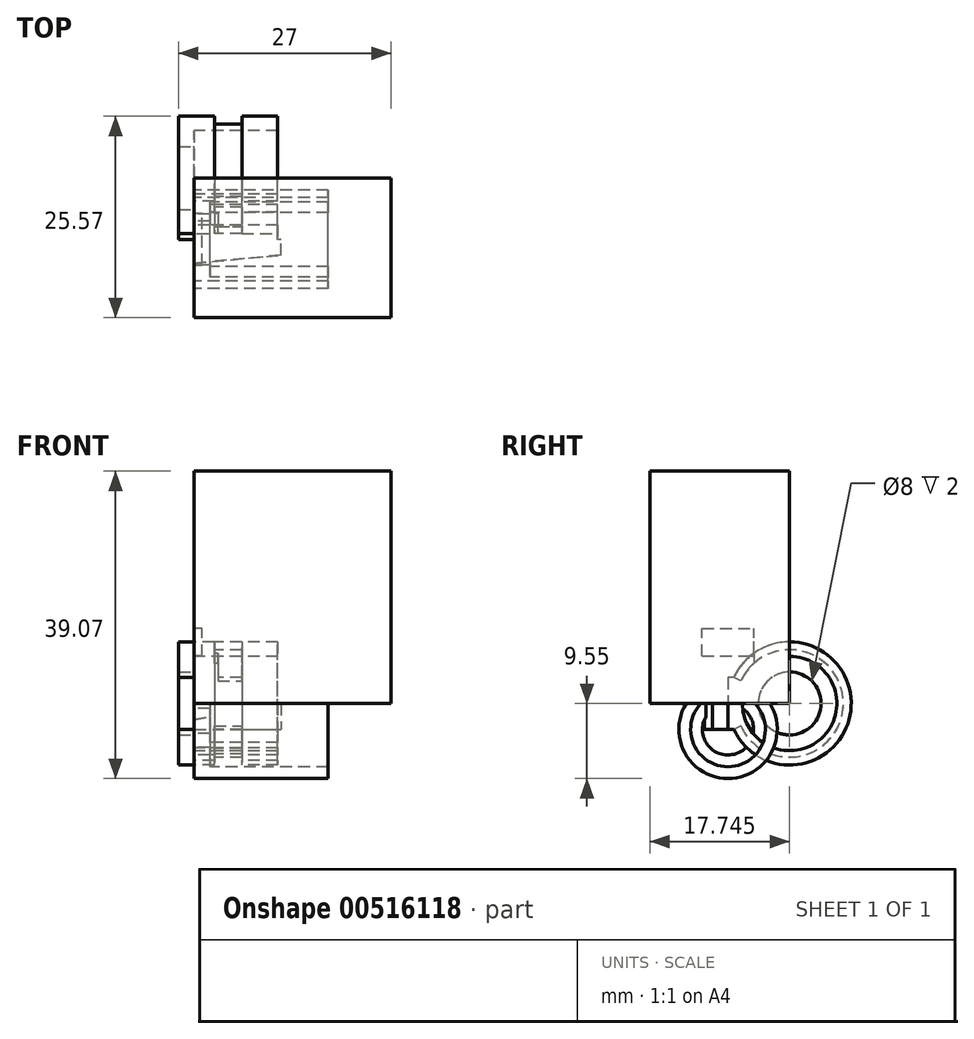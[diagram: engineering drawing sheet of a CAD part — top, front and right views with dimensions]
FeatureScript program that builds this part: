
annotation { "Feature Type Name" : "Feature", "Feature Type Description" : "" }
export const myFeature = defineFeature(function(context is Context, id is Id, definition is map)
    precondition{}
    {
        {
            var Q0;
            Q0=qCreatedBy(makeId("Top.planeOp"),FACE);
            var sketch = newSketch(context, id + "F0", { "sketchPlane" : qUnion([Q0])});
            skLineSegment(sketch, "E0", {"start": v(0, 0) * mm, "end": v(11, 0) * mm});
            skLineSegment(sketch, "E1", {"start": v(11, 0) * mm, "end": v(11, -2) * mm});
            skLineSegment(sketch, "E2", {"start": v(0, 0) * mm, "end": v(0, -3) * mm});
            skLineSegment(sketch, "E3", {"start": v(0, -3) * mm, "end": v(11, -2) * mm});
            skSolve(sketch);
        }
        {
            var Q0;
            Q0=makeQuery(id+"F0.imprint","IMPRINT",FACE,{"disambiguationData":[TD([[makeQuery(id+"F0.imprint","IMPRINT",EDGE,{"derivedFrom":sQuery(id+"F0.wireOp",EDGE,"E0")}),-1.0]])]});
            extrude(context, id + "F1", {"entities" : qUnion([Q0]), "depth" : 6.6 * mm, "offsetDistance" : 25 * mm});
        }
        {
            var Q0;
            Q0=qCreatedBy(makeId("Right.planeOp"),FACE);
            var sketch = newSketch(context, id + "F2", { "sketchPlane" : qUnion([Q0])});
            skLineSegment(sketch, "E4.0", {"start": v(0, 6.6) * mm, "end": v(0, 0) * mm});
            skLineSegment(sketch, "E5", {"start": v(0, 3.3) * mm, "end": v(7.83, 3.3) * mm, "construction": true});
            skCircle(sketch, "E6", {"center": v(7.83, 3.3) * mm, "radius": 7.83 * mm});
            skCircle(sketch, "E7", {"center": v(7.83, 3.3) * mm, "radius": 6 * mm});
            skCircle(sketch, "E8", {"center": v(7.83, 3.3) * mm, "radius": 4 * mm});
            skSolve(sketch);
        }
        {
            var Q0;
            Q0=makeQuery(id+"F2.imprint","IMPRINT",FACE,{"disambiguationData":[TD([[makeQuery(id+"F2.imprint","IMPRINT",EDGE,{"derivedFrom":sQuery(id+"F2.wireOp",EDGE,"E6")}),1.0]])]});
            extrude(context, id + "F3", {"entities" : qUnion([Q0]), "depth" : 10.6 * mm, "offsetDistance" : 25 * mm});
        }
        {
            var Q0;
            Q0=makeQuery(id+"F2.imprint","IMPRINT",FACE,{"disambiguationData":[TD([[makeQuery(id+"F2.imprint","IMPRINT",EDGE,{"derivedFrom":sQuery(id+"F2.wireOp",EDGE,"E7")}),1.0]])]});
            var Q1;
            Q1=makeQuery(id+"F2.imprint","IMPRINT",FACE,{"disambiguationData":[TD([[makeQuery(id+"F2.imprint","IMPRINT",EDGE,{"derivedFrom":sQuery(id+"F2.wireOp",EDGE,"E6")}),1.0]])]});
            extrude(context, id + "F4", {"entities" : qUnion([Q0, Q1]), "operationType" : NewBodyOperationType.ADD, "oppositeDirection" : true, "depth" : 2 * mm, "offsetDistance" : 25 * mm});
        }
        {
            var Q0;
            Q0=qCreatedBy(makeId("Top.planeOp"),FACE);
            var sketch = newSketch(context, id + "F5", { "sketchPlane" : qUnion([Q0])});
            skLineSegment(sketch, "E9.0", {"start": v(-2, 15.65) * mm, "end": v(-2, 0) * mm});
            skLineSegment(sketch, "E9.1", {"start": v(10.6, 15.65) * mm, "end": v(10.6, 0) * mm});
            skLineSegment(sketch, "E10", {"start": v(-2, 15.65) * mm, "end": v(10.6, 15.65) * mm});
            skLineSegment(sketch, "E11.bottom", {"start": v(6.05, 14.65) * mm, "end": v(2.55, 14.65) * mm});
            skLineSegment(sketch, "E11.top", {"start": v(6.05, 16.65) * mm, "end": v(2.55, 16.65) * mm});
            skLineSegment(sketch, "E11.left", {"start": v(6.05, 14.65) * mm, "end": v(6.05, 16.65) * mm});
            skLineSegment(sketch, "E11.right", {"start": v(2.55, 14.65) * mm, "end": v(2.55, 16.65) * mm});
            skPoint(sketch, "E11.middle", {"position": v(4.3, 15.65) * mm});
            skSolve(sketch);
        }
        {
            var Q0;
            Q0=qCreatedBy(makeId("Right.planeOp"),FACE);
            var sketch = newSketch(context, id + "F6", { "sketchPlane" : qUnion([Q0])});
            skPoint(sketch, "E12.0", {"position": v(7.83, 3.3) * mm});
            skLineSegment(sketch, "E13.bottom", {"start": v(7.82, 3.3) * mm, "end": v(-9.92, 3.3) * mm});
            skLineSegment(sketch, "E13.top", {"start": v(7.82, 32.82) * mm, "end": v(-9.92, 32.82) * mm});
            skLineSegment(sketch, "E13.left", {"start": v(7.83, 3.3) * mm, "end": v(7.83, 32.82) * mm});
            skLineSegment(sketch, "E13.right", {"start": v(-9.92, 3.3) * mm, "end": v(-9.92, 32.82) * mm});
            skSolve(sketch);
        }
        {
            var Q0;
            Q0=makeQuery(id+"F6.imprint","IMPRINT",FACE,{"disambiguationData":[TD([[makeQuery(id+"F6.imprint","IMPRINT",EDGE,{"derivedFrom":sQuery(id+"F6.wireOp",EDGE,"E13.bottom")}),-1.0]])]});
            extrude(context, id + "F7", {"entities" : qUnion([Q0]), "depth" : 25 * mm, "offsetDistance" : 25 * mm});
        }
        {
            var Q0;
            Q0=makeQuery(id+"F7.opExtrude","SWEPT_FACE",FACE,{"disambiguationData":[OSD([sQuery(id+"F6.wireOp",EDGE,"E13.bottom")])]});
            var sketch = newSketch(context, id + "F8", { "sketchPlane" : qUnion([Q0])});
            skLineSegment(sketch, "E14.0.0", {"start": v(6.05, -15.65) * mm, "end": v(2.55, -15.65) * mm});
            skLineSegment(sketch, "E14.0.1", {"start": v(2.55, -15.65) * mm, "end": v(2.55, -14.65) * mm});
            skLineSegment(sketch, "E14.0.2", {"start": v(2.55, -14.65) * mm, "end": v(6.05, -14.65) * mm});
            skLineSegment(sketch, "E14.0.3", {"start": v(6.05, -14.65) * mm, "end": v(6.05, -15.65) * mm});
            skSolve(sketch);
        }
        {
            var Q0;
            Q0=makeQuery(id+"F8.imprint","IMPRINT",FACE,{"disambiguationData":[TD([[makeQuery(id+"F8.imprint","IMPRINT",EDGE,{"derivedFrom":sQuery(id+"F8.wireOp",EDGE,"E14.0.0")}),-1.0]])]});
            var Q1;
            Q1=makeQuery(id+"F7.opExtrude","SWEPT_EDGE",EDGE,{"disambiguationData":[OSD([sQuery(id+"F6.wireOp",EDGE,"E13.bottom"),sQuery(id+"F6.wireOp",EDGE,"E13.left")])]});
            revolve(context, id + "F9", {"operationType" : NewBodyOperationType.REMOVE, "entities" : qUnion([Q0]), "axis" : qUnion([Q1]), "revolveType" : RevolveType.TWO_DIRECTIONS, "oppositeDirection" : true, "angle" : 155 * degree, "angleBack" : 205 * degree});
        }
        {
            var Q0;
            Q0=makeQuery(id+"F3.opExtrude","CAP_FACE",FACE,{"disambiguationData":[OSD([sQuery(id+"F2.wireOp",EDGE,"E6"),sQuery(id+"F2.wireOp",EDGE,"E7")])],"isStart":false});
            var sketch = newSketch(context, id + "F10", { "sketchPlane" : qUnion([Q0])});
            skPoint(sketch, "E15.0", {"position": v(0.73, 6.6) * mm});
            skPoint(sketch, "E15.1", {"position": v(0.73, 0) * mm});
            skLineSegment(sketch, "E16", {"start": v(0.73, 6.6) * mm, "end": v(0, 6.6) * mm});
            skLineSegment(sketch, "E17", {"start": v(0, 6.6) * mm, "end": v(0, 0) * mm});
            skLineSegment(sketch, "E18", {"start": v(0, 0) * mm, "end": v(0.73, 0) * mm});
            skLineSegment(sketch, "E19", {"start": v(0.73, 0) * mm, "end": v(0.73, 6.6) * mm});
            skSolve(sketch);
        }
        {
            var Q0;
            {var subQ0=sQuery(id+"F10.wireOp",EDGE,"E19");Q0=makeQuery(id+"F10.imprint","IMPRINT",FACE,{"disambiguationData":[TD([[makeQuery(id+"F10.imprint","IMPRINT",EDGE,{"derivedFrom":subQ0}),1.0]])]});}
            var Q1;
            {var subQ0=sQuery(id+"F10.wireOp",EDGE,"E16");Q1=makeQuery(id+"F10.imprint","IMPRINT",FACE,{"disambiguationData":[TD([[makeQuery(id+"F10.imprint","IMPRINT",EDGE,{"derivedFrom":subQ0}),1.0]])]});}
            var Q2;
            {var subQ0=sQuery(id+"F10.wireOp",EDGE,"E18");Q2=makeQuery(id+"F10.imprint","IMPRINT",FACE,{"disambiguationData":[TD([[makeQuery(id+"F10.imprint","IMPRINT",EDGE,{"derivedFrom":subQ0}),1.0]])]});}
            var Q3;
            Q3=makeQuery(id+"F4.opExtrude","CAP_FACE",FACE,{"disambiguationData":[OSD([sQuery(id+"F2.wireOp",EDGE,"E6"),sQuery(id+"F2.wireOp",EDGE,"E8")])],"isStart":false});
            extrude(context, id + "F11", {"entities" : qUnion([Q0, Q1, Q2]), "operationType" : NewBodyOperationType.ADD, "endBound" : BoundingType.UP_TO_SURFACE, "oppositeDirection" : true, "depth" : 25 * mm, "endBoundEntityFace" : qUnion([Q3]), "offsetDistance" : 25 * mm});
        }
        {
            var Q0;
            Q0=qCreatedBy(makeId("Right.planeOp"),FACE);
            var sketch = newSketch(context, id + "F12", { "sketchPlane" : qUnion([Q0])});
            skCircle(sketch, "E20", {"center": v(0, 0) * mm, "radius": 4.75 * mm});
            skCircle(sketch, "E21", {"center": v(0, 0) * mm, "radius": 6.25 * mm});
            skCircle(sketch, "E22", {"center": v(0, 0) * mm, "radius": 3.25 * mm});
            skSolve(sketch);
        }
        {
            var Q0;
            Q0=makeQuery(id+"F12.imprint","IMPRINT",FACE,{"disambiguationData":[TD([[makeQuery(id+"F12.imprint","IMPRINT",EDGE,{"derivedFrom":sQuery(id+"F12.wireOp",EDGE,"E20")}),-1.0]])]});
            extrude(context, id + "F13", {"entities" : qUnion([Q0]), "depth" : 17 * mm, "offsetDistance" : 25 * mm});
        }
        {
            var Q0;
            Q0=makeQuery(id+"F12.imprint","IMPRINT",FACE,{"disambiguationData":[TD([[makeQuery(id+"F12.imprint","IMPRINT",EDGE,{"derivedFrom":sQuery(id+"F12.wireOp",EDGE,"E20")}),1.0]])]});
            extrude(context, id + "F14", {"entities" : qUnion([Q0]), "operationType" : NewBodyOperationType.ADD, "depth" : 2 * mm, "offsetDistance" : 25 * mm});
        }
        {
            var Q0;
            Q0=makeQuery(id+"F13.opExtrude","CAP_FACE",FACE,{"disambiguationData":[OSD([sQuery(id+"F12.wireOp",EDGE,"E20"),sQuery(id+"F12.wireOp",EDGE,"E21")])],"isStart":false});
            var sketch = newSketch(context, id + "F15", { "sketchPlane" : qUnion([Q0])});
            skPoint(sketch, "E23", {"position": v(-6.25, 0) * mm});
            skPoint(sketch, "E24", {"position": v(6.25, 0) * mm});
            skLineSegment(sketch, "E25.bottom", {"start": v(-6.25, 0) * mm, "end": v(6.25, 0) * mm});
            skLineSegment(sketch, "E25.top", {"start": v(-6.25, 16.25) * mm, "end": v(6.25, 16.25) * mm});
            skLineSegment(sketch, "E25.left", {"start": v(-6.25, 0) * mm, "end": v(-6.25, 16.25) * mm});
            skLineSegment(sketch, "E25.right", {"start": v(6.25, 0) * mm, "end": v(6.25, 16.25) * mm});
            skSolve(sketch);
        }
        {
            var Q0;
            Q0=makeQuery(id+"F12.imprint","IMPRINT",FACE,{"disambiguationData":[TD([[makeQuery(id+"F12.imprint","IMPRINT",EDGE,{"derivedFrom":sQuery(id+"F12.wireOp",EDGE,"E20")}),-1.0]])]});
            var sketch = newSketch(context, id + "F16", { "sketchPlane" : qUnion([Q0])});
            skArc(sketch, "E26.0.0", {"start": v(-6.25, 0) * mm, "mid": v(0, 6.25) * mm, "end": v(6.25, 0) * mm});
            skLineSegment(sketch, "E26.0.1", {"start": v(6.25, 0) * mm, "end": v(6.25, 16.25) * mm});
            skLineSegment(sketch, "E26.0.2", {"start": v(6.25, 16.25) * mm, "end": v(-6.25, 16.25) * mm});
            skLineSegment(sketch, "E26.0.3", {"start": v(-6.25, 16.25) * mm, "end": v(-6.25, 0) * mm});
            skSolve(sketch);
        }
        {
            var Q0;
            Q0=makeQuery(id+"F16.imprint","IMPRINT",FACE,{"disambiguationData":[TD([[makeQuery(id+"F16.imprint","IMPRINT",EDGE,{"derivedFrom":sQuery(id+"F16.wireOp",EDGE,"E26.0.0")}),-1.0]])]});
            var sketch = newSketch(context, id + "F17", { "sketchPlane" : qUnion([Q0])});
            skLineSegment(sketch, "E27.bottom", {"start": v(-6.33, 12.82) * mm, "end": v(6.33, 12.82) * mm});
            skLineSegment(sketch, "E27.top", {"start": v(-6.33, 9.32) * mm, "end": v(6.33, 9.32) * mm});
            skLineSegment(sketch, "E27.left", {"start": v(-6.33, 12.82) * mm, "end": v(-6.33, 9.32) * mm});
            skLineSegment(sketch, "E27.right", {"start": v(6.33, 12.82) * mm, "end": v(6.33, 9.32) * mm});
            skLineSegment(sketch, "E28.bottom", {"start": v(-3.3, 5.4) * mm, "end": v(3.3, 5.4) * mm});
            skLineSegment(sketch, "E28.top", {"start": v(-3.3, 27.25) * mm, "end": v(3.3, 27.25) * mm});
            skLineSegment(sketch, "E28.left", {"start": v(-3.3, 5.4) * mm, "end": v(-3.3, 27.25) * mm});
            skLineSegment(sketch, "E28.right", {"start": v(3.3, 5.4) * mm, "end": v(3.3, 27.25) * mm});
            skPoint(sketch, "E28.middle", {"position": v(0, 16.32) * mm});
            skSolve(sketch);
        }
        {
            var Q0;
            {var subQ0=sQuery(id+"F17.wireOp",EDGE,"E28.left");var subQ1=sQuery(id+"F17.wireOp",EDGE,"E27.bottom");var subQ2=makeQuery(id+"F17.imprint","INTERSECT",VERTEX,{"derivedFrom":[subQ1,subQ0]});Q0=makeQuery(id+"F17.imprint","IMPRINT",FACE,{"disambiguationData":[TD([[makeQuery(id+"F17.imprint","IMPRINT",EDGE,{"disambiguationData":[TD([[subQ2,-1.0]])],"derivedFrom":subQ1}),-1.0]])]});}
            var Q1;
            {var subQ0=sQuery(id+"F17.wireOp",EDGE,"E28.left");var subQ1=sQuery(id+"F17.wireOp",EDGE,"E27.bottom");var subQ2=makeQuery(id+"F17.imprint","INTERSECT",VERTEX,{"derivedFrom":[subQ1,subQ0]});Q1=makeQuery(id+"F17.imprint","IMPRINT",FACE,{"disambiguationData":[TD([[makeQuery(id+"F17.imprint","IMPRINT",EDGE,{"disambiguationData":[TD([[subQ2,-1.0]])],"derivedFrom":subQ1}),1.0]])]});}
            var Q2;
            {var subQ0=sQuery(id+"F17.wireOp",EDGE,"E28.left");var subQ1=sQuery(id+"F17.wireOp",EDGE,"E27.top");var subQ2=makeQuery(id+"F17.imprint","INTERSECT",VERTEX,{"derivedFrom":[subQ1,subQ0]});Q2=makeQuery(id+"F17.imprint","IMPRINT",FACE,{"disambiguationData":[TD([[makeQuery(id+"F17.imprint","IMPRINT",EDGE,{"disambiguationData":[TD([[subQ2,-1.0]])],"derivedFrom":subQ1}),-1.0]])]});}
            extrude(context, id + "F18", {"entities" : qUnion([Q0, Q1, Q2]), "operationType" : NewBodyOperationType.ADD, "depth" : 3 * mm, "offsetDistance" : 25 * mm});
        }
        {
            var Q0;
            {var subQ0=sQuery(id+"F17.wireOp",EDGE,"E28.left");var subQ1=sQuery(id+"F17.wireOp",EDGE,"E27.bottom");var subQ2=makeQuery(id+"F17.imprint","INTERSECT",VERTEX,{"derivedFrom":[subQ1,subQ0]});Q0=makeQuery(id+"F17.imprint","IMPRINT",FACE,{"disambiguationData":[TD([[makeQuery(id+"F17.imprint","IMPRINT",EDGE,{"disambiguationData":[TD([[subQ2,-1.0]])],"derivedFrom":subQ1}),-1.0]])]});}
            extrude(context, id + "F19", {"entities" : qUnion([Q0]), "operationType" : NewBodyOperationType.REMOVE, "depth" : 1 * mm, "offsetDistance" : 25 * mm});
        }
    });
